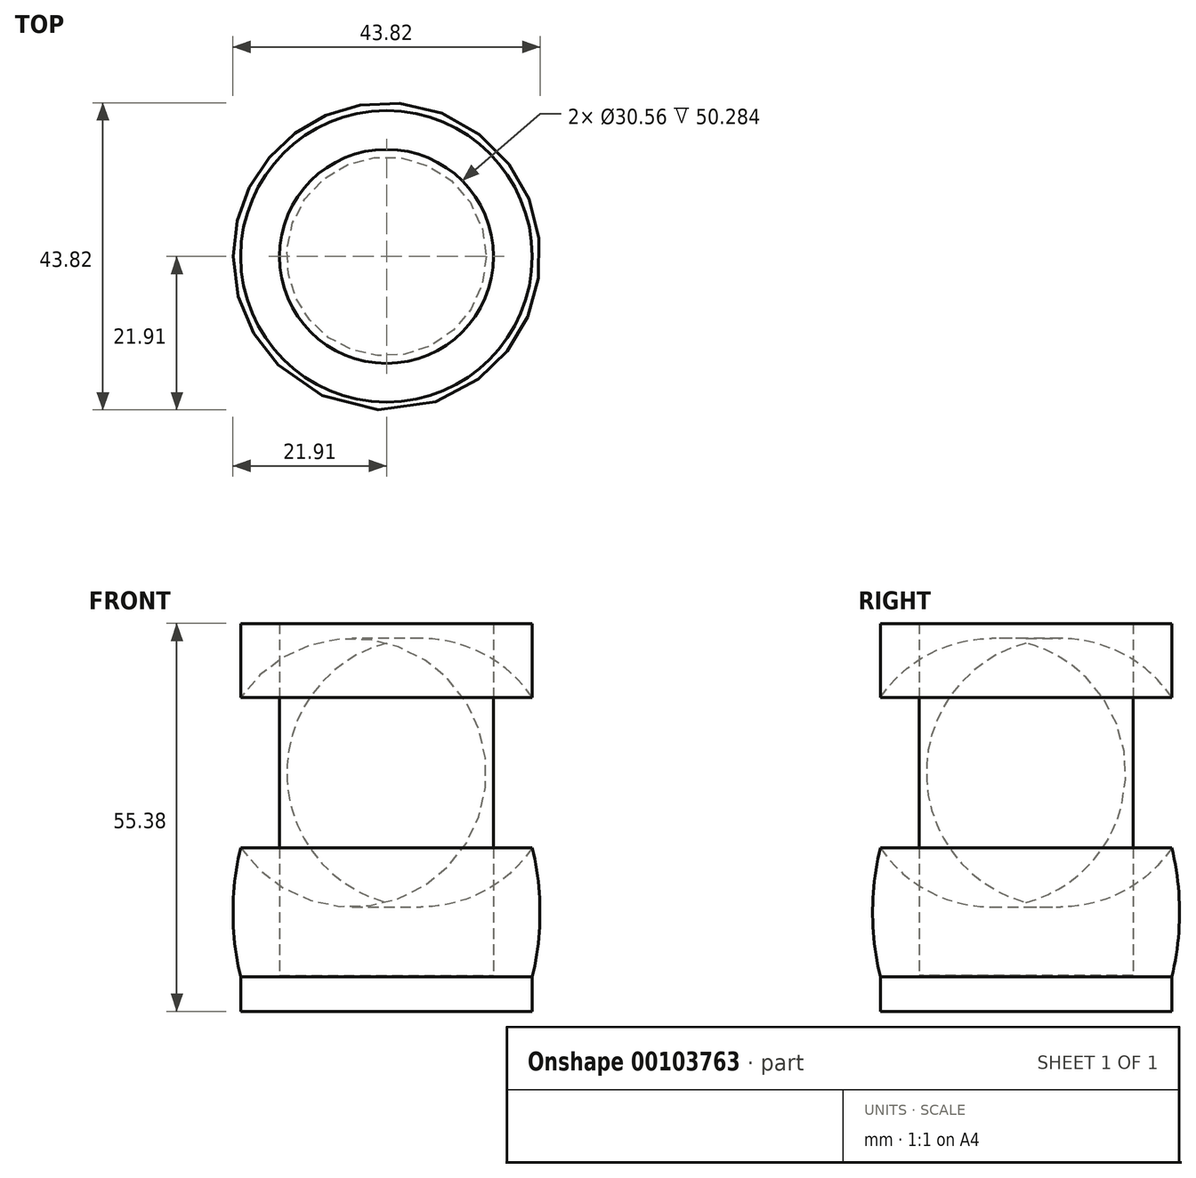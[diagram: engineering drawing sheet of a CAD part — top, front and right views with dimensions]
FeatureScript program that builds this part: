
annotation { "Feature Type Name" : "Feature", "Feature Type Description" : "" }
export const myFeature = defineFeature(function(context is Context, id is Id, definition is map)
    precondition{}
    {
        {
            var Q0;
            Q0=qCreatedBy(makeId("Front.planeOp"),FACE);
            var sketch = newSketch(context, id + "F0", { "sketchPlane" : qUnion([Q0])});
            skLineSegment(sketch, "E0", {"start": v(0, 0) * mm, "end": v(0, 55.38) * mm});
            skLineSegment(sketch, "E1", {"start": v(0, 0) * mm, "end": v(20.8, 0) * mm});
            skLineSegment(sketch, "E2", {"start": v(20.8, 0) * mm, "end": v(20.8, 4.9) * mm});
            skArc(sketch, "E3", {"start": v(20.8, 4.9) * mm, "mid": v(21.9, 14.12) * mm, "end": v(20.8, 23.35) * mm});
            skArc(sketch, "E4", {"start": v(20.8, 23.35) * mm, "mid": v(24.09, 34.07) * mm, "end": v(20.8, 44.79) * mm});
            skLineSegment(sketch, "E5", {"start": v(20.8, 44.79) * mm, "end": v(20.8, 55.38) * mm});
            skLineSegment(sketch, "E6", {"start": v(20.8, 55.38) * mm, "end": v(15.28, 55.38) * mm});
            skLineSegment(sketch, "E7", {"start": v(15.28, 55.38) * mm, "end": v(15.28, 5.1) * mm});
            skLineSegment(sketch, "E8", {"start": v(15.28, 5.1) * mm, "end": v(0, 5.1) * mm});
            skSolve(sketch);
        }
        {
            var Q0;
            Q0 = qSketchRegion(id + "F0", true);
            var Q1;
            Q1=sQuery(id+"F0.wireOp",EDGE,"E0");
            revolve(context, id + "F1", {"entities" : qUnion([Q0]), "axis" : qUnion([Q1]), "revolveType" : RevolveType.FULL});
        }
        {
            var Q0;
            Q0 = qSketchRegion(id + "F0", true);
            var Q1;
            Q1=sQuery(id+"F0.wireOp",EDGE,"E0");
            revolve(context, id + "F2", {"entities" : qUnion([Q0]), "axis" : qUnion([Q1]), "revolveType" : RevolveType.FULL});
        }
    });
